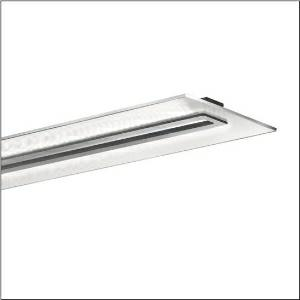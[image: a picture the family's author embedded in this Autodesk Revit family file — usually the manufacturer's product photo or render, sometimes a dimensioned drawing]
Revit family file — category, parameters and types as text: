
# Revit family: vega_r__11_5mn238dle_9bfa
name_source: partatom
category: Lighting Fixtures
units: mm (PartAtom-declared; Revit-internal decimal feet)

## family parameters
Cut with Voids When Loaded = No
Host = Face
Light Source = No
Part Type = Normal
Room Calculation Point = No
Round Connector Dimension = Use Diameter
Shared = No

## types (1)
- --- (1 x LED 4000K / CRI = 80 (unbekannt), 8130 lm, 4000K)
    Apparent Load = 62 VA
    CIE Flux Codes = 61 86 97 62 100
    Color Rendering = 80
    Color Temperature = 4000K
    Default Elevation = 1800 mm
    Description = Vega® 11, office luminaire, primary light control with prismatic reflector, of PMMA, transparent prismatic structure, CAT 2 (L<= 1500cd/m²), light emission: direct/indirect distribution, primary light characteristic: symmetric, installation type: suspended mounting, surface-mounted, LED, rated luminous flux: 8.130lm, luminous efficacy: 131lm/W, light colour: 840, colour temperature: 4000K, control gear: DALI, with terminal, 3+2-pole, max. 2.5mm², mains connection: 230V, AC, 50Hz, connection cable inclusive, cable length: 1,5m, rated input power: 62W, luminaire housing, rectangular, rounded, of aluminium section, anodised, metallic grey (RAL 9006), length: 1.250mm, width: 350mm, height: 43mm, luminaire housing, lower part, of aluminium section, anodised, metallic grey (RAL 9006), of PC, grey, protection rating (complete): IP20, insulation class (complete): insulation class I (protective earthing), certification: CE, standard: EN 50419, packaging unit: 1 piece
    Height = 40 mm  [stored 0.131234 ft]
    Lamp = 1 x LED 4000K / CRI >= 80 (unbekannt)
    Lamp Light Flux = 8130 lm
    Lamp count = 1
    Length = 1250 mm
    Luminous efficacy = 131 lm/W
    Manufacturer = Siteco
    ModVariant = No
    Model = 5MN238DLE
    Mounting Place = Ceiling
    Mounting Type = Pendant
    Number of Poles = 1
    OnlyDefault = Yes
    Power Factor = 1
    Product Name = Vega® 11
    Product group = office luminaire | ceiling pendant
    ProductGroupID = 904
    Protection Class = Protection class I
    Protection Degree = IP 20
    RLX_Detail_Level = 1
    RLX_Emergency_Light_Flux = 0 lm
    RLX_Emergency_Type = 0
    RLX_Emergency_Type_DB = No
    RlxData = <blob elided: 62889 chars, md5=9037df3d>
    Socket = socket
    Standby Power = 0 W
    System Light Flux = 8130 lm
    System Power = 62 W
    Type Comments = factory setting: luminous flux: 100 % | dim-lin: 254 | 458 mA
    Type Image = l_1004807.jpg
    URL = http://relux.com
    VarID = @adj_204052
    Voltage = 0 V
    Weight = 0.00 kg
    Width = 350 mm

note: [stored X ft] marks values corroborated as IEEE doubles in the binary element streams (Revit-internal decimal feet)

## geometry (parser evidence)
native form markers: Blend x4, Sweep x13
no freeform markers — native parametric forms only
